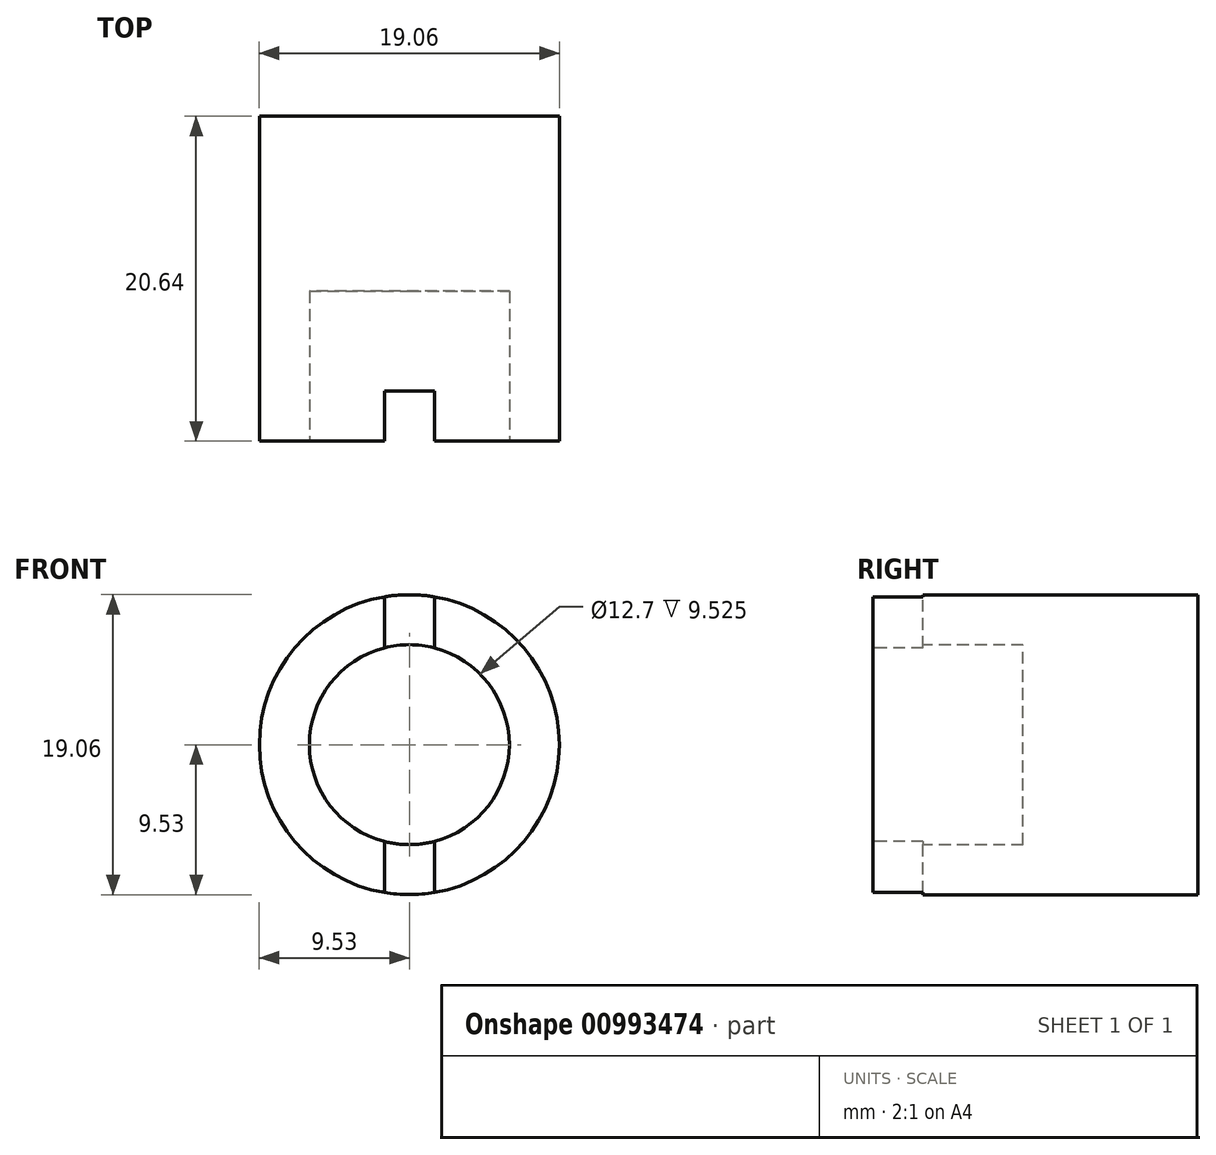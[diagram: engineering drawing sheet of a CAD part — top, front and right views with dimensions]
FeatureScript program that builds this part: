
annotation { "Feature Type Name" : "Feature", "Feature Type Description" : "" }
export const myFeature = defineFeature(function(context is Context, id is Id, definition is map)
    precondition{}
    {
        {
            var Q0;
            Q0=qCreatedBy(makeId("Front.planeOp"),FACE);
            var sketch = newSketch(context, id + "F0", { "sketchPlane" : qUnion([Q0])});
            skLineSegment(sketch, "E0.bottom", {"start": v(9.53, -9.52) * mm, "end": v(-9.53, -9.53) * mm});
            skLineSegment(sketch, "E0.top", {"start": v(9.53, 9.53) * mm, "end": v(-9.53, 9.52) * mm});
            skLineSegment(sketch, "E0.left", {"start": v(9.53, -9.52) * mm, "end": v(9.53, 9.53) * mm});
            skLineSegment(sketch, "E0.right", {"start": v(-9.53, -9.53) * mm, "end": v(-9.53, 9.52) * mm});
            skPoint(sketch, "E0.middle", {"position": v(0, 0) * mm});
            skSolve(sketch);
        }
        {
            var Q0;
            Q0=makeQuery(id+"F0.imprint","IMPRINT",FACE,{"disambiguationData":[TD([[makeQuery(id+"F0.imprint","IMPRINT",EDGE,{"derivedFrom":sQuery(id+"F0.wireOp",EDGE,"E0.bottom")}),-1.0]])]});
            extrude(context, id + "F1", {"entities" : qUnion([Q0]), "depth" : 20.64 * mm, "offsetDistance" : 25.4 * mm});
        }
        {
            var Q0;
            Q0=makeQuery(id+"F1.opExtrude","CAP_FACE",FACE,{"disambiguationData":[OSD([sQuery(id+"F0.wireOp",EDGE,"E0.bottom"),sQuery(id+"F0.wireOp",EDGE,"E0.top"),sQuery(id+"F0.wireOp",EDGE,"E0.left"),sQuery(id+"F0.wireOp",EDGE,"E0.right")])],"isStart":false});
            var sketch = newSketch(context, id + "F2", { "sketchPlane" : qUnion([Q0])});
            skCircle(sketch, "E1", {"center": v(0, 0) * mm, "radius": 6.35 * mm});
            skSolve(sketch);
        }
        {
            var Q0;
            Q0=makeQuery(id+"F2.imprint","IMPRINT",FACE,{"disambiguationData":[TD([[makeQuery(id+"F2.imprint","IMPRINT",EDGE,{"derivedFrom":sQuery(id+"F2.wireOp",EDGE,"E1")}),1.0]])]});
            extrude(context, id + "F3", {"entities" : qUnion([Q0]), "operationType" : NewBodyOperationType.REMOVE, "oppositeDirection" : true, "depth" : 9.52 * mm, "offsetDistance" : 25.4 * mm});
        }
        {
            var Q0;
            Q0=makeQuery(id+"F1.opExtrude","SWEPT_FACE",FACE,{"disambiguationData":[OSD([sQuery(id+"F0.wireOp",EDGE,"E0.top")])]});
            var sketch = newSketch(context, id + "F4", { "sketchPlane" : qUnion([Q0])});
            skLineSegment(sketch, "E2", {"start": v(0, -20.64) * mm, "end": v(-1.59, -20.64) * mm});
            skLineSegment(sketch, "E3", {"start": v(-1.59, -20.64) * mm, "end": v(1.59, -20.64) * mm});
            skLineSegment(sketch, "E4", {"start": v(1.59, -20.64) * mm, "end": v(1.59, -17.46) * mm});
            skLineSegment(sketch, "E5", {"start": v(-1.59, -20.64) * mm, "end": v(-1.59, -17.46) * mm});
            skLineSegment(sketch, "E6", {"start": v(-1.59, -17.46) * mm, "end": v(1.59, -17.46) * mm});
            skSolve(sketch);
        }
        {
            var Q0;
            {var subQ0=sQuery(id+"F4.wireOp",EDGE,"E4");Q0=makeQuery(id+"F4.imprint","IMPRINT",FACE,{"disambiguationData":[TD([[makeQuery(id+"F4.imprint","IMPRINT",EDGE,{"derivedFrom":subQ0}),1.0]])]});}
            extrude(context, id + "F5", {"entities" : qUnion([Q0]), "operationType" : NewBodyOperationType.REMOVE, "oppositeDirection" : true, "depth" : 25.4 * mm, "offsetDistance" : 25.4 * mm});
        }
        {
            var Q0;
            Q0=makeQuery(id+"F1.opExtrude","CAP_FACE",FACE,{"disambiguationData":[OSD([sQuery(id+"F0.wireOp",EDGE,"E0.bottom"),sQuery(id+"F0.wireOp",EDGE,"E0.top"),sQuery(id+"F0.wireOp",EDGE,"E0.left"),sQuery(id+"F0.wireOp",EDGE,"E0.right")])],"isStart":true});
            var sketch = newSketch(context, id + "F6", { "sketchPlane" : qUnion([Q0])});
            skCircle(sketch, "E7", {"center": v(0, 0) * mm, "radius": 9.53 * mm});
            skSolve(sketch);
        }
        {
            var Q0;
            {var subQ0=sQuery(id+"F6.wireOp",EDGE,"E7");var subQ1=makeQuery(id+"F1.opExtrude","CAP_EDGE",EDGE,{"disambiguationData":[OSD([sQuery(id+"F0.wireOp",EDGE,"E0.top")])],"isStart":true});var subQ2=makeQuery(id+"F6.imprint","INTERSECT",VERTEX,{"derivedFrom":[subQ1,subQ0]});Q0=makeQuery(id+"F6.imprint","IMPRINT",FACE,{"disambiguationData":[TD([[makeQuery(id+"F6.imprint","IMPRINT",EDGE,{"disambiguationData":[TD([[subQ2,-1.0]])],"derivedFrom":subQ0}),-1.0]])]});}
            var Q1;
            {var subQ0=sQuery(id+"F6.wireOp",EDGE,"E7");var subQ1=makeQuery(id+"F1.opExtrude","CAP_EDGE",EDGE,{"disambiguationData":[OSD([sQuery(id+"F0.wireOp",EDGE,"E0.top")])],"isStart":true});var subQ2=makeQuery(id+"F6.imprint","INTERSECT",VERTEX,{"derivedFrom":[subQ1,subQ0]});Q1=makeQuery(id+"F6.imprint","IMPRINT",FACE,{"disambiguationData":[TD([[makeQuery(id+"F6.imprint","IMPRINT",EDGE,{"disambiguationData":[TD([[subQ2,1.0]])],"derivedFrom":subQ0}),-1.0]])]});}
            var Q2;
            {var subQ0=sQuery(id+"F6.wireOp",EDGE,"E7");var subQ1=makeQuery(id+"F1.opExtrude","CAP_EDGE",EDGE,{"disambiguationData":[OSD([sQuery(id+"F0.wireOp",EDGE,"E0.left")])],"isStart":true});var subQ2=makeQuery(id+"F6.imprint","INTERSECT",VERTEX,{"derivedFrom":[subQ1,subQ0]});Q2=makeQuery(id+"F6.imprint","IMPRINT",FACE,{"disambiguationData":[TD([[makeQuery(id+"F6.imprint","IMPRINT",EDGE,{"disambiguationData":[TD([[subQ2,-1.0]])],"derivedFrom":subQ0}),-1.0]])]});}
            var Q3;
            {var subQ0=sQuery(id+"F6.wireOp",EDGE,"E7");var subQ1=makeQuery(id+"F1.opExtrude","CAP_EDGE",EDGE,{"disambiguationData":[OSD([sQuery(id+"F0.wireOp",EDGE,"E0.right")])],"isStart":true});var subQ2=makeQuery(id+"F6.imprint","INTERSECT",VERTEX,{"derivedFrom":[subQ1,subQ0]});Q3=makeQuery(id+"F6.imprint","IMPRINT",FACE,{"disambiguationData":[TD([[makeQuery(id+"F6.imprint","IMPRINT",EDGE,{"disambiguationData":[TD([[subQ2,1.0]])],"derivedFrom":subQ0}),-1.0]])]});}
            extrude(context, id + "F7", {"entities" : qUnion([Q0, Q1, Q2, Q3]), "operationType" : NewBodyOperationType.REMOVE, "oppositeDirection" : true, "depth" : 25.4 * mm, "offsetDistance" : 25.4 * mm});
        }
    });
